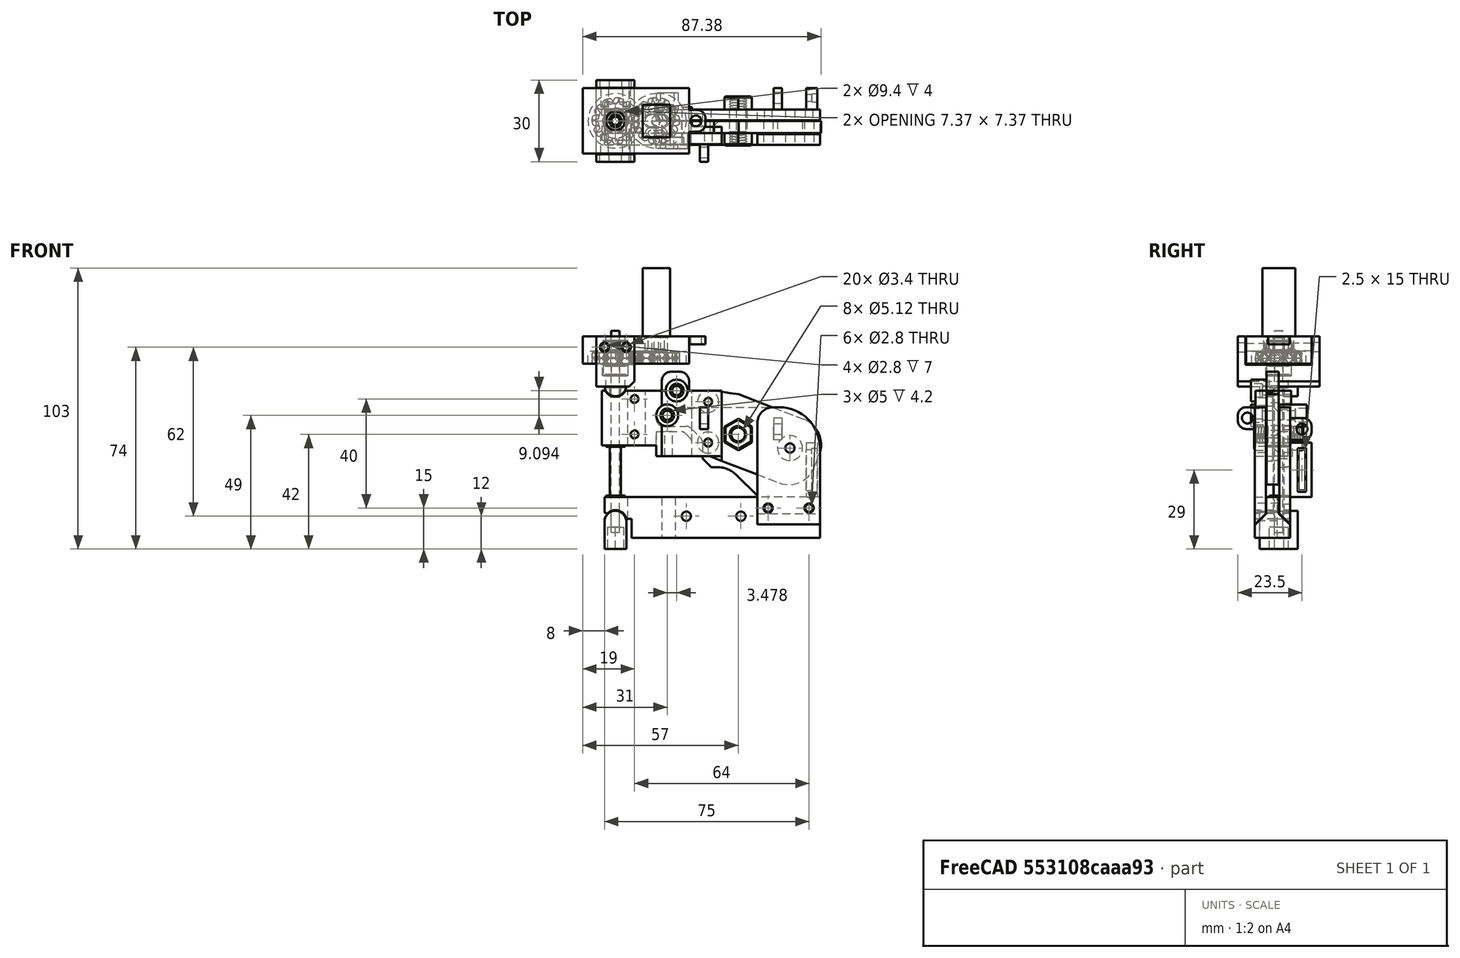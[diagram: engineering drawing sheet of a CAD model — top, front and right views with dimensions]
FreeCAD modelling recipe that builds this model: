
FCSTD DOCUMENT  (FreeCAD 0.17R13528 (Git))
Label: guillotine
License: All rights reserved
LicenseURL: http://en.wikipedia.org/wiki/All_rights_reserved
objects: Part::Cylinder×82, Part::MultiFuse×54, Part::Cut×51, Part::Box×48, Part::Feature×20, Part::Chamfer×14, Part::Fillet×10, Part::Mirroring×9, Part::MultiCommon×3, App::DocumentObjectGroup×3, Part::Fuse×2
note: 293 computed .brp shape members not serialized (recipe doc carries the construction recipe); baked Part::Feature solids carry a one-line shape summary decoded from their .brp

FEATURE [Part::Box] Box001027033  label="Cube053"
  AttacherType = Attacher::AttachEngine3D
  Height = 25
  Length = 40
  Placement = pos=(32,-4.5,-33) rot=(0,1,0;0.366519rad)
  Width = 4.5
FEATURE [Part::Box] Box001027045154  label="Cube202"
  AttacherType = Attacher::AttachEngine3D
  Height = 24
  Length = 47
  Placement = pos=(-5,-4.5,-34) rot=(0,1,0;0rad)
  Width = 4.5
FEATURE [Part::Box] Box001027045159  label="Cube207"
  AttacherType = Attacher::AttachEngine3D
  Height = 10
  Length = 20
  Placement = pos=(29,-6,-9) rot=(0,1,0;0.139626rad)
  Width = 10
FEATURE [Part::Cylinder] Cylinder210  label="cutter-fit-cylinder001"
  Angle = 360
  AttacherType = Attacher::AttachEngine3D
  Height = 21
  Placement = pos=(45,5,-26) rot=(1,0,0;1.5708rad)
  Radius = 3.2
FEATURE [Part::Box] Box001027045161  label="Cube209"
  AttacherType = Attacher::AttachEngine3D
  Height = 15
  Length = 30
  Placement = pos=(-10,-7,-57) rot=(0,0,1;0rad)
  Width = 15
FEATURE [Part::Feature] Part__Feature069020  label="M6 thread016"
  Placement = pos=(45,-4,-26) rot=(0.935113,0.250563,-0.250563;1.63783rad)
  shape: bbox 10 x 5.798 x 11.55 mm, 23 faces (baked)
FEATURE [Part::MultiFuse] Fusion112112  label="move-arm-1"
  Shapes = -> [Box001027033,Box001027045154]
FEATURE [Part::Cut] Cut190  label="move-arm-2"
  Base = -> Fusion112112
  Tool = -> Box001027045159
FEATURE [Part::Cut] Cut191  label="move-arm-3"
  Base = -> Cut190
  Tool = -> Cylinder210
FEATURE [Part::MultiFuse] Fusion112113  label="move-arm-4"
  Shapes = -> [Cut191,Part__Feature069020]
FEATURE [Part::Cylinder] Cylinder214  label="bearing-fit-cylinder001"
  Angle = 360
  AttacherType = Attacher::AttachEngine3D
  Height = 21
  Placement = pos=(64,5,-31) rot=(1,0,0;1.5708rad)
  Radius = 4.6
FEATURE [Part::Cut] Cut192  label="move-arm-5"
  Base = -> Fusion112113
  Placement = pos=(-6.44714,0,-21.2943) rot=(0,-1,0;0.314159rad)
  Tool = -> Cylinder214
FEATURE [Part::Cut] Cut193  label="move-arm-6"
  Base = -> Cut192
  Placement = pos=(12.7119,0,18.2598) rot=(0,1,0;0.314159rad)
  Tool = -> Box001027045161
FEATURE [Part::Box] Box001027045166  label="Cube214"
  AttacherType = Attacher::AttachEngine3D
  Height = 35
  Length = 46
  Placement = pos=(-7,-7,-36) rot=(0,0,1;0rad)
  Width = 32
FEATURE [Part::Box] Box001027045167  label="Cube215"
  AttacherType = Attacher::AttachEngine3D
  Height = 44
  Length = 12
  Placement = pos=(28,-2.25,-41) rot=(0,0,1;0rad)
  Width = 31
FEATURE [Part::Cut] Cut202
  Base = -> Box001027045166
  Tool = -> Box001027045167
FEATURE [Part::Cut] Cut208
  Base = -> Cut193
  Tool = -> Cut202
FEATURE [Part::Box] Box001027045174  label="Cube222"
  AttacherType = Attacher::AttachEngine3D
  Height = 24
  Length = 22
  Placement = pos=(17,-8.5,-34) rot=(0,0,1;0rad)
  Width = 4
FEATURE [Part::Cylinder] Cylinder226  label="M3-clearance001"
  Angle = 360
  AttacherType = Attacher::AttachEngine3D
  Height = 20
  Placement = pos=(34,5,-14) rot=(1,0,0;1.5708rad)
  Radius = 1.7
FEATURE [Part::Cylinder] Cylinder227  label="M3-clearance002"
  Angle = 360
  AttacherType = Attacher::AttachEngine3D
  Height = 20
  Placement = pos=(34,5,-29) rot=(1,0,0;1.5708rad)
  Radius = 1.7
FEATURE [Part::Cylinder] Cylinder230  label="M3-tap005"
  Angle = 360
  AttacherType = Attacher::AttachEngine3D
  Height = 20
  Placement = pos=(34,5,-14) rot=(1,0,0;1.5708rad)
  Radius = 1.4
FEATURE [Part::Cylinder] Cylinder231  label="M3-tap006"
  Angle = 360
  AttacherType = Attacher::AttachEngine3D
  Height = 20
  Placement = pos=(34,5,-29) rot=(1,0,0;1.5708rad)
  Radius = 1.4
FEATURE [Part::MultiFuse] Fusion112121
  Shapes = -> [Cylinder226,Cylinder227]
FEATURE [Part::MultiFuse] Fusion112123
  Shapes = -> [Cylinder230,Cylinder231]
FEATURE [Part::Cut] Cut210  label="cutter-arm-1"
  Base = -> Cut208
  Tool = -> Fusion112121
FEATURE [Part::Chamfer] Chamfer021
  Base = -> Cut210
  Edges = 1 edges r=2.2: [Edge107]
FEATURE [Part::Chamfer] Chamfer022
  Base = -> Chamfer021
  Edges = 3 edges r=2.2: [Edge5,Edge20,Edge21]
FEATURE [Part::Fillet] Fillet041  label="cutting-arm"
  Base = -> Chamfer022
  Edges = 2 edges r=10: [Edge49,Edge58]
FEATURE [Part::Box] Box001027011  label="Cube031"
  AttacherType = Attacher::AttachEngine3D
  Height = 43
  Length = 40
  Placement = pos=(35,0.2,-59) rot=(0,0,1;0rad)
  Width = 4
FEATURE [Part::Cylinder] Cylinder074  label="cutter-fit-cylinder"
  Angle = 360
  AttacherType = Attacher::AttachEngine3D
  Height = 21
  Placement = pos=(45,5,-26) rot=(1,0,0;1.5708rad)
  Radius = 3.2
FEATURE [Part::Box] Box001027030  label="Cube050"
  AttacherType = Attacher::AttachEngine3D
  Height = 12
  Length = 25
  Placement = pos=(18,-5,-42) rot=(0,0,1;0rad)
  Width = 9.5
FEATURE [Part::Chamfer] Chamfer010
  Base = -> Box001027030
  Edges = 2 edges r=5: [Edge2,Edge6]
FEATURE [Part::Fillet] Fillet025  label="Adjuster-hole"
  Base = -> Chamfer010
  Edges = 4 edges r=3: [Edge2,Edge10,Edge17,Edge18]
  Placement = pos=(-11,0,7) rot=(0,0,1;0rad)
FEATURE [Part::Box] Box001027045147  label="Cube195"
  AttacherType = Attacher::AttachEngine3D
  Height = 43
  Length = 23
  Placement = pos=(52,-8.8,-59) rot=(0,0,1;0rad)
  Width = 4
FEATURE [Part::Box] Box001027045148  label="Cube196"
  AttacherType = Attacher::AttachEngine3D
  Height = 26
  Length = 29
  Placement = pos=(23,-2,-64) rot=(0,0,1;0rad)
  Width = 10
FEATURE [Part::Box] Box001027045149  label="Cube197"
  AttacherType = Attacher::AttachEngine3D
  Height = 15
  Length = 79
  Placement = pos=(-4,-8.8,-64) rot=(0,0,1;0rad)
  Width = 13
FEATURE [Part::Cut] Cut172
  Base = -> Box001027011
  Tool = -> Box001027045148
FEATURE [Part::Cylinder] Cylinder197  label="rocker-cut001"
  Angle = 360
  AttacherType = Attacher::AttachEngine3D
  Height = 18
  Placement = pos=(0,7,-58) rot=(1,0,0;1.5708rad)
  Radius = 4.2
FEATURE [Part::Box] Box001027045150  label="Cube198"
  AttacherType = Attacher::AttachEngine3D
  Height = 15
  Length = 20
  Placement = pos=(-14,-11.8,-72) rot=(0,0,1;0rad)
  Width = 18
FEATURE [Part::MultiFuse] Fusion112098
  Shapes = -> [Box001027045150,Cylinder197]
FEATURE [Part::Cut] Cut173
  Base = -> Box001027045149
  Tool = -> Fusion112098
FEATURE [Part::Chamfer] Chamfer017
  Base = -> Cut173
  Edges = 1 edges r=2: [Edge4]
FEATURE [Part::Box] Box001027045151  label="Cube199"
  AttacherType = Attacher::AttachEngine3D
  Height = 43
  Length = 41
  Placement = pos=(35,0,-59) rot=(0,0,1;0rad)
  Width = 7
FEATURE [Part::Box] Box001027045152  label="Cube200"
  AttacherType = Attacher::AttachEngine3D
  Height = 43
  Length = 25
  Placement = pos=(52,-10.6,-59) rot=(0,0,1;0rad)
  Width = 6
FEATURE [Part::Box] Box001027045153  label="Cube201"
  AttacherType = Attacher::AttachEngine3D
  Height = 26
  Length = 29
  Placement = pos=(23,-2,-64) rot=(0,0,1;0rad)
  Width = 10
FEATURE [Part::Cut] Cut174
  Base = -> Box001027045151
  Tool = -> Box001027045153
FEATURE [Part::MultiFuse] Fusion112099
  Shapes = -> [Box001027045152,Cut174]
FEATURE [Part::Cut] Cut175
  Base = -> Chamfer017
  Tool = -> Fusion112099
FEATURE [Part::Cylinder] Cylinder198  label="Cylinder242"
  Angle = 360
  AttacherType = Attacher::AttachEngine3D
  Height = 20
  Placement = pos=(56,8,-54) rot=(1,0,0;1.5708rad)
  Radius = 1.7
FEATURE [Part::Cylinder] Cylinder199  label="Cylinder243"
  Angle = 360
  AttacherType = Attacher::AttachEngine3D
  Height = 20
  Placement = pos=(71,8,-54) rot=(1,0,0;1.5708rad)
  Radius = 1.7
FEATURE [Part::Cylinder] Cylinder200  label="Cylinder244"
  Angle = 360
  AttacherType = Attacher::AttachEngine3D
  Height = 20
  Placement = pos=(56,8,-54) rot=(1,0,0;1.5708rad)
  Radius = 1.7
FEATURE [Part::Cylinder] Cylinder201  label="Cylinder245"
  Angle = 360
  AttacherType = Attacher::AttachEngine3D
  Height = 20
  Placement = pos=(71,8,-54) rot=(1,0,0;1.5708rad)
  Radius = 1.7
FEATURE [Part::Cylinder] Cylinder202  label="Cylinder246"
  Angle = 360
  AttacherType = Attacher::AttachEngine3D
  Height = 20
  Placement = pos=(56,8,-54) rot=(1,0,0;1.5708rad)
  Radius = 1.4
FEATURE [Part::Cylinder] Cylinder203  label="Cylinder247"
  Angle = 360
  AttacherType = Attacher::AttachEngine3D
  Height = 20
  Placement = pos=(71,8,-54) rot=(1,0,0;1.5708rad)
  Radius = 1.4
FEATURE [Part::MultiFuse] Fusion112100
  Placement = pos=(0,0,1) rot=(0,0,1;0rad)
  Shapes = -> [Cylinder198,Cylinder199]
FEATURE [Part::MultiFuse] Fusion112101
  Placement = pos=(0,0,1) rot=(0,0,1;0rad)
  Shapes = -> [Cylinder200,Cylinder201]
FEATURE [Part::MultiFuse] Fusion112102
  Placement = pos=(0,0,1) rot=(0,0,1;0rad)
  Shapes = -> [Cylinder202,Cylinder203]
FEATURE [Part::Cut] Cut176
  Base = -> Cut175
  Tool = -> Fusion112100
FEATURE [Part::Cut] Cut177
  Base = -> Box001027045147
  Tool = -> Fusion112101
FEATURE [Part::Cut] Cut178
  Base = -> Cut172
  Tool = -> Fusion112102
FEATURE [Part::Cylinder] Cylinder204  label="Cylinder248"
  Angle = 360
  AttacherType = Attacher::AttachEngine3D
  Height = 20
  Placement = pos=(26,8,-54) rot=(1,0,0;1.5708rad)
  Radius = 1.7
FEATURE [Part::Cylinder] Cylinder205  label="Cylinder249"
  Angle = 360
  AttacherType = Attacher::AttachEngine3D
  Height = 20
  Placement = pos=(46,8,-54) rot=(1,0,0;1.5708rad)
  Radius = 1.7
FEATURE [Part::MultiFuse] Fusion112103
  Placement = pos=(0,0,-2) rot=(0,0,1;0rad)
  Shapes = -> [Cylinder204,Cylinder205]
FEATURE [Part::Cut] Cut179
  Base = -> Cut176
  Tool = -> Fusion112103
FEATURE [Part::Box] Box001027045157  label="Cube205"
  AttacherType = Attacher::AttachEngine3D
  Height = 18
  Length = 40
  Placement = pos=(15,0.2,-34) rot=(0,0,1;0rad)
  Width = 4
FEATURE [Part::MultiFuse] Fusion112104
  Shapes = -> [Cut178,Box001027045157]
FEATURE [Part::Chamfer] Chamfer019
  Base = -> Fusion112104
  Edges = 1 edges r=3.9: [Edge12]
FEATURE [Part::Chamfer] Chamfer020
  Base = -> Chamfer019
  Edges = 1 edges r=10.5: [Edge31]
FEATURE [Part::Cut] Cut180
  Base = -> Chamfer020
  Tool = -> Fillet025
FEATURE [Part::Cylinder] Cylinder209  label="Cylinder253"
  Angle = 360
  AttacherType = Attacher::AttachEngine3D
  Height = 30
  Placement = pos=(19.5,2,-70) rot=(0,0,1;0rad)
  Radius = 2.5
FEATURE [Part::Box] Box001027045160  label="Cube208"
  AttacherType = Attacher::AttachEngine3D
  Height = 21
  Length = 5
  Placement = pos=(17,2,-68) rot=(0,0,1;0rad)
  Width = 10
FEATURE [Part::MultiFuse] Fusion112106
  Shapes = -> [Cylinder209,Box001027045160]
FEATURE [Part::Cut] Cut184
  Base = -> Cut179
  Tool = -> Fusion112106
FEATURE [Part::Cut] Cut186
  Base = -> Cut180
  Tool = -> Cylinder074
FEATURE [Part::Feature] Part__Feature069021  label="M6 thread017"
  Placement = pos=(45,-4,-26) rot=(0.935113,0.250563,-0.250563;1.63783rad)
  shape: bbox 10 x 5.798 x 11.55 mm, 23 faces (baked)
FEATURE [Part::Mirroring] Part__Mirroring014  label="M6 thread017 (Mirror #14)"
  Base = (0,0,0)
  Normal = (0,1,0)
  Source = -> Part__Feature069021
FEATURE [Part::MultiFuse] Fusion112109
  Shapes = -> [Cut186,Part__Mirroring014]
FEATURE [Part::Cylinder] Cylinder211  label="Cylinder254"
  Angle = 360
  AttacherType = Attacher::AttachEngine3D
  Height = 74
  Placement = pos=(0,0,-62) rot=(0,0,1;0rad)
  Radius = 2
FEATURE [Part::Box] Box001027045163  label="Cube211"
  AttacherType = Attacher::AttachEngine3D
  Height = 60
  Length = 10
  Placement = pos=(-10,-2,-57) rot=(0,0,1;0rad)
  Width = 4
FEATURE [Part::MultiFuse] Fusion112110
  Placement = pos=(2.5,0,0) rot=(0,0,1;0rad)
  Shapes = -> [Cylinder211,Box001027045163]
FEATURE [Part::Cut] Cut189  label="base-and-mount-b"
  Base = -> Cut184
  Tool = -> Fusion112110
FEATURE [Part::Cylinder] Cylinder222  label="bearing-fit-cylinder002"
  Angle = 360
  AttacherType = Attacher::AttachEngine3D
  Height = 21
  Placement = pos=(64,5,-31) rot=(1,0,0;1.5708rad)
  Radius = 1.7
FEATURE [Part::Cylinder] Cylinder223  label="bearing-fit-cylinder003"
  Angle = 360
  AttacherType = Attacher::AttachEngine3D
  Height = 21
  Placement = pos=(64,5,-31) rot=(1,0,0;1.5708rad)
  Radius = 1.7
FEATURE [Part::Cut] Cut200
  Base = -> Fusion112109
  Tool = -> Cylinder222
FEATURE [Part::Cut] Cut201
  Base = -> Cut177
  Tool = -> Cylinder223
FEATURE [Part::Fillet] Fillet033
  Base = -> Cut200
  Edges = 1 edges r=15: [Edge111]
FEATURE [Part::Fillet] Fillet034
  Base = -> Cut201
  Edges = 1 edges r=15: [Edge12]
FEATURE [Part::Fillet] Fillet035
  Base = -> Fillet033
  Edges = 2 edges r=2.5: [Edge63,Edge65]
FEATURE [Part::Fillet] Fillet038  label="bearing-support-1a"
  Base = -> Fillet034
  Edges = 1 edges r=6: [Edge17]
FEATURE [Part::Fillet] Fillet039  label="bearing-support-2a"
  Base = -> Fillet035
  Edges = 1 edges r=10: [Edge65]
FEATURE [Part::Chamfer] Chamfer026
  Base = -> Cut189
  Edges = 1 edges r=4: [Edge73]
FEATURE [Part::Chamfer] Chamfer027  label="base-and-mount"
  Base = -> Chamfer026
  Edges = 1 edges r=4: [Edge34]
FEATURE [Part::Chamfer] Chamfer028  label="bearing-support-1"
  Base = -> Fillet038
  Edges = 1 edges r=3.9: [Edge21]
FEATURE [Part::Chamfer] Chamfer029  label="bearing-support-2a001"
  Base = -> Fillet039
  Edges = 1 edges r=3.9: [Edge5]
FEATURE [Part::Box] Box  label="Cube"
  AttacherType = Attacher::AttachEngine3D
  Height = 20
  Length = 4
  Placement = pos=(0,-10,-10) rot=(0,0,1;0rad)
  Width = 20
FEATURE [Part::Feature] Part__Feature027  label="1310"
  Placement = pos=(2,0,0) rot=(0,0,1;0rad)
  shape: bbox 13.32 x 18 x 18 mm, 178 faces (baked)
FEATURE [Part::Cylinder] Cylinder
  Angle = 360
  AttacherType = Attacher::AttachEngine3D
  Height = 25
  Placement = pos=(-4,0,0) rot=(0,1,0;1.5708rad)
  Radius = 5
FEATURE [Part::Cylinder] Cylinder001
  Angle = 360
  AttacherType = Attacher::AttachEngine3D
  Height = 10
  Placement = pos=(-2,0,0) rot=(0,1,0;1.5708rad)
  Radius = 1.7
FEATURE [Part::MultiFuse] Fusion
  Shapes = -> [Part__Feature027,Cylinder]
FEATURE [Part::MultiCommon] Common  label="gear-blank"
  Shapes = -> [Fusion,Box]
FEATURE [Part::Feature] Part__Feature028  label="1310001"
  Placement = pos=(2,0,0) rot=(0,0,1;0rad)
  shape: bbox 13.32 x 18 x 18 mm, 178 faces (baked)
FEATURE [Part::Cut] Cut  label="shaft-gear-a"
  Base = -> Common
  Placement = pos=(0,0,0) rot=(0,-1,0;1.5708rad)
  Tool = -> Cylinder001
FEATURE [Part::Box] Box002  label="Cube002"
  AttacherType = Attacher::AttachEngine3D
  Height = 10
  Length = 15
  Placement = pos=(-4,-6,1) rot=(0,0,1;0rad)
  Width = 10
FEATURE [Part::Cylinder] Cylinder002
  Angle = 360
  AttacherType = Attacher::AttachEngine3D
  Height = 25
  Placement = pos=(-4,0,0) rot=(0,1,0;1.5708rad)
  Radius = 5
FEATURE [Part::MultiFuse] Fusion001
  Shapes = -> [Part__Feature028,Cylinder002]
FEATURE [Part::Cylinder] Cylinder003
  Angle = 360
  AttacherType = Attacher::AttachEngine3D
  Height = 10
  Placement = pos=(-2,0,0) rot=(0,1,0;1.5708rad)
  Radius = 1.8
FEATURE [Part::Cut] Cut001
  Base = -> Cylinder003
  Tool = -> Box002
FEATURE [Part::Fuse] Fusion003
FEATURE [Part::Cylinder] Cylinder012
  Angle = 360
  AttacherType = Attacher::AttachEngine3D
  Height = 10
  Placement = pos=(5,-4.5,0) rot=(0,1,0;1.5708rad)
  Radius = 0.8
FEATURE [Part::Fuse] Fusion048  label="motor"
  Base = -> Cylinder012
  Placement = pos=(15,0,0) rot=(0,-1,0;1.5708rad)
  Tool = -> Fusion003
FEATURE [Part::Box] Box001  label="Cube001"
  AttacherType = Attacher::AttachEngine3D
  Height = 20
  Length = 4
  Placement = pos=(0,-10,-10) rot=(0,0,1;0rad)
  Width = 20
FEATURE [Part::MultiCommon] Common001  label="gear-blank001"
  Shapes = -> [Fusion001,Box001]
FEATURE [Part::Cut] Cut002  label="motor-gear"
  Base = -> Common001
  Placement = pos=(15,0,4) rot=(0,1,0;1.5708rad)
  Tool = -> Cut001
FEATURE [Part::Feature] Part__Feature035  label="423001001"
  Placement = pos=(0,0,-2) rot=(0,0,1;3.74342rad)
  shape: bbox 9 x 9 x 4 mm, 22 faces (baked)
FEATURE [Part::Feature] Part__Feature066  label="212001001001"
  Placement = pos=(0,0,0) rot=(0.905883,0.423527,0;3.14159rad)
  shape: bbox 7 x 7 x 0.5 mm, 6 faces (baked)
FEATURE [Part::Cylinder] Cylinder013
  Angle = 360
  AttacherType = Attacher::AttachEngine3D
  Height = 74
  Placement = pos=(0,0,-62) rot=(0,0,1;0rad)
  Radius = 1.5
FEATURE [Part::Cylinder] Cylinder014
  Angle = 360
  AttacherType = Attacher::AttachEngine3D
  Height = 8
  Placement = pos=(0,0,1) rot=(0,0,1;0rad)
  Radius = 4
FEATURE [Part::Box] Box003  label="Cube003"
  AttacherType = Attacher::AttachEngine3D
  Height = 10
  Length = 10
  Placement = pos=(-12.85,-5,0) rot=(0,0,1;0rad)
  Width = 10
FEATURE [Part::Feature] Box001001
  Placement = pos=(-2.09487,-13.6284,0) rot=(0,0,1;1.0472rad)
  shape: bbox 13.66 x 13.66 x 10 mm, 6 faces (baked)
FEATURE [Part::Feature] Box001002
  Placement = pos=(10.7551,-8.62843,0) rot=(0,0,1;2.0944rad)
  shape: bbox 13.66 x 13.66 x 10 mm, 6 faces (baked)
FEATURE [Part::Feature] Box001003
  Placement = pos=(12.85,5,0) rot=(0,0,1;3.14159rad)
  shape: bbox 10 x 10 x 10 mm, 6 faces (baked)
FEATURE [Part::Feature] Box001004
  Placement = pos=(2.09487,13.6284,0) rot=(0,0,1;4.18879rad)
  shape: bbox 13.66 x 13.66 x 10 mm, 6 faces (baked)
FEATURE [Part::Feature] Box001005
  Placement = pos=(-10.7551,8.62843,0) rot=(0,0,-1;1.0472rad)
  shape: bbox 13.66 x 13.66 x 10 mm, 6 faces (baked)
FEATURE [Part::MultiFuse] Fusion049
  Shapes = -> [Box003,Box001005,Box001001,Box001002,Box001003,Box001004]
FEATURE [Part::Cut] Cut003  label="m3-nut"
  Base = -> Cylinder014
  Placement = pos=(0,0,1) rot=(0,0,1;0rad)
  Tool = -> Fusion049
FEATURE [Part::Feature] Part__Feature067  label="423001001001"
  Placement = pos=(0,0,7) rot=(0,0,1;3.74342rad)
  shape: bbox 9 x 9 x 4 mm, 22 faces (baked)
FEATURE [Part::Cylinder] Cylinder015
  Angle = 360
  AttacherType = Attacher::AttachEngine3D
  Height = 100
  Placement = pos=(0,0,-12) rot=(0,0,1;0rad)
  Radius = 1.7
FEATURE [Part::MultiFuse] Fusion050
  Shapes = -> [Cylinder015,Cut003]
FEATURE [Part::Cut] Cut004  label="shaft-gear"
  Base = -> Cut
  Tool = -> Fusion050
FEATURE [Part::Box] Box001006  label="Cube004"
  AttacherType = Attacher::AttachEngine3D
  Height = 10
  Length = 39
  Placement = pos=(-12,-12,0) rot=(0,0,1;0rad)
  Width = 24
FEATURE [Part::Cylinder] Cylinder016
  Angle = 360
  AttacherType = Attacher::AttachEngine3D
  Height = 30
  Placement = pos=(0,0,-12) rot=(0,0,1;0rad)
  Radius = 3.5
FEATURE [Part::Cylinder] Cylinder017
  Angle = 360
  AttacherType = Attacher::AttachEngine3D
  Height = 30
  Placement = pos=(0,0,-21.5) rot=(0,0,1;0rad)
  Radius = 4.7
FEATURE [Part::Cylinder] Cylinder018
  Angle = 360
  AttacherType = Attacher::AttachEngine3D
  Height = 30
  Placement = pos=(0,0,-25.5) rot=(0,0,1;0rad)
  Radius = 10
FEATURE [Part::Cylinder] Cylinder019
  Angle = 360
  AttacherType = Attacher::AttachEngine3D
  Height = 30
  Placement = pos=(16,0,-25.5) rot=(0,0,1;0rad)
  Radius = 10
FEATURE [Part::Cylinder] Cylinder020
  Angle = 360
  AttacherType = Attacher::AttachEngine3D
  Height = 30
  Placement = pos=(17,0,-12.5) rot=(0,0,1;0rad)
  Radius = 2.1
FEATURE [Part::Cylinder] Cylinder021
  Angle = 360
  AttacherType = Attacher::AttachEngine3D
  Height = 30
  Placement = pos=(17,-4.5,-12.5) rot=(0,0,1;0rad)
  Radius = 1
FEATURE [Part::Cylinder] Cylinder022
  Angle = 360
  AttacherType = Attacher::AttachEngine3D
  Height = 30
  Placement = pos=(17,4.5,-12.5) rot=(0,0,1;0rad)
  Radius = 1
FEATURE [Part::Cylinder] Cylinder023
  Angle = 360
  AttacherType = Attacher::AttachEngine3D
  Height = 30
  Placement = pos=(13,0,-12.5) rot=(0,0,1;0rad)
  Radius = 2.1
FEATURE [Part::Cylinder] Cylinder024
  Angle = 360
  AttacherType = Attacher::AttachEngine3D
  Height = 30
  Placement = pos=(13,-4.5,-12.5) rot=(0,0,1;0rad)
  Radius = 1
FEATURE [Part::Cylinder] Cylinder025
  Angle = 360
  AttacherType = Attacher::AttachEngine3D
  Height = 30
  Placement = pos=(13,4.5,-12.5) rot=(0,0,1;0rad)
  Radius = 1
FEATURE [Part::Box] Box001007  label="Cube005"
  AttacherType = Attacher::AttachEngine3D
  Height = 27
  Length = 4
  Placement = pos=(13,-2.1,-11) rot=(0,0,1;0rad)
  Width = 4.2
FEATURE [Part::Box] Box001008  label="Cube006"
  AttacherType = Attacher::AttachEngine3D
  Height = 27
  Length = 4
  Placement = pos=(13,-5.5,-11) rot=(0,0,1;0rad)
  Width = 2
FEATURE [Part::Box] Box001009  label="Cube007"
  AttacherType = Attacher::AttachEngine3D
  Height = 27
  Length = 4
  Placement = pos=(13,3.5,-11) rot=(0,0,1;0rad)
  Width = 2
FEATURE [Part::MultiFuse] Fusion052  label="motor-slots"
  Shapes = -> [Box001009,Cylinder021,Cylinder022,Box001007,Cylinder020,Cylinder023,Cylinder024,Box001008,Cylinder025]
FEATURE [Part::Cylinder] Cylinder026
  Angle = 360
  AttacherType = Attacher::AttachEngine3D
  Height = 30
  Placement = pos=(15,0,-25.5) rot=(0,0,1;0rad)
  Radius = 10
FEATURE [Part::MultiFuse] Fusion053  label="gearbox-cavity-1"
  Shapes = -> [Cylinder019,Cylinder016,Cylinder017,Cylinder018,Cylinder026]
FEATURE [Part::MultiFuse] Fusion054  label="gearbox-cavity-2"
  Shapes = -> [Fusion053,Fusion052]
FEATURE [Part::Cut] Cut005  label="gearbox-1"
  Base = -> Box001006
  Tool = -> Fusion054
FEATURE [Part::Chamfer] Chamfer  label="gearbox-2"
  Base = -> Cut005
  Edges = 10 edges r=1: [Edge47,Edge50,Edge52,Edge54,Edge55,Edge58,Edge60,Edge62,Edge64,Edge65]
FEATURE [Part::Box] Box001010  label="Cube008"
  AttacherType = Attacher::AttachEngine3D
  Height = 8
  Length = 14
  Placement = pos=(-7,-15,-8.5) rot=(0,0,1;0rad)
  Width = 30
FEATURE [Part::Box] Box001011  label="Cube009"
  AttacherType = Attacher::AttachEngine3D
  Height = 11
  Length = 14
  Placement = pos=(-7,-15,-1) rot=(0,0,1;0rad)
  Width = 2.8
FEATURE [Part::Box] Box001012  label="Cube010"
  AttacherType = Attacher::AttachEngine3D
  Height = 11
  Length = 14
  Placement = pos=(-7,12.2,-1) rot=(0,0,1;0rad)
  Width = 2.8
FEATURE [Part::MultiFuse] Fusion055  label="bearing-clamp-1"
  Shapes = -> [Box001010,Box001012,Box001011]
FEATURE [Part::Cylinder] Cylinder027  label="M3-tap-1"
  Angle = 360
  AttacherType = Attacher::AttachEngine3D
  Height = 19
  Placement = pos=(-4,24,6) rot=(1,0,0;1.5708rad)
  Radius = 1.4
FEATURE [Part::Cylinder] Cylinder028  label="M3-tap-2"
  Angle = 360
  AttacherType = Attacher::AttachEngine3D
  Height = 19
  Placement = pos=(4,24,6) rot=(1,0,0;1.5708rad)
  Radius = 1.4
FEATURE [Part::Cylinder] Cylinder029  label="M3-clear-1"
  Angle = 360
  AttacherType = Attacher::AttachEngine3D
  Height = 19
  Placement = pos=(-4,24,6) rot=(1,0,0;1.5708rad)
  Radius = 1.7
FEATURE [Part::Cylinder] Cylinder030  label="M3-clear-2"
  Angle = 360
  AttacherType = Attacher::AttachEngine3D
  Height = 19
  Placement = pos=(4,24,6) rot=(1,0,0;1.5708rad)
  Radius = 1.7
FEATURE [Part::Cylinder] Cylinder031  label="M3-tap-003"
  Angle = 360
  AttacherType = Attacher::AttachEngine3D
  Height = 19
  Placement = pos=(-4,24,6) rot=(1,0,0;1.5708rad)
  Radius = 1.4
FEATURE [Part::Cylinder] Cylinder032  label="M3-tap-004"
  Angle = 360
  AttacherType = Attacher::AttachEngine3D
  Height = 19
  Placement = pos=(4,24,6) rot=(1,0,0;1.5708rad)
  Radius = 1.4
FEATURE [Part::Cylinder] Cylinder033  label="M3-clear-003"
  Angle = 360
  AttacherType = Attacher::AttachEngine3D
  Height = 19
  Placement = pos=(4,24,6) rot=(1,0,0;1.5708rad)
  Radius = 1.7
FEATURE [Part::Cylinder] Cylinder034  label="M3-clear-004"
  Angle = 360
  AttacherType = Attacher::AttachEngine3D
  Height = 19
  Placement = pos=(-4,24,6) rot=(1,0,0;1.5708rad)
  Radius = 1.7
FEATURE [Part::Mirroring] Part__Mirroring  label="M3-tap-003 (Mirror #1)"
  Base = (0,0,0)
  Normal = (0,1,0)
  Source = -> Cylinder031
FEATURE [Part::Mirroring] Part__Mirroring001  label="M3-tap-004 (Mirror #2)"
  Base = (0,0,0)
  Normal = (0,1,0)
  Source = -> Cylinder032
FEATURE [Part::Mirroring] Part__Mirroring002  label="M3-clear-003 (Mirror #3)"
  Base = (0,0,0)
  Normal = (0,1,0)
  Source = -> Cylinder033
FEATURE [Part::Mirroring] Part__Mirroring003  label="M3-clear-004 (Mirror #4)"
  Base = (0,0,0)
  Normal = (0,1,0)
  Source = -> Cylinder034
FEATURE [Part::MultiFuse] Fusion056  label="M3-tap-a"
  Shapes = -> [Cylinder027,Cylinder028,Part__Mirroring,Part__Mirroring001]
FEATURE [Part::MultiFuse] Fusion057  label="M3-clear-a"
  Shapes = -> [Cylinder029,Cylinder030,Part__Mirroring002,Part__Mirroring003]
FEATURE [Part::Cut] Cut006  label="bearing-clamp-2"
  Base = -> Fusion055
  Tool = -> Fusion057
FEATURE [Part::Cut] Cut007  label="gearbox-3"
  Base = -> Chamfer
  Tool = -> Fusion056
FEATURE [Part::Cylinder] Cylinder035
  Angle = 360
  AttacherType = Attacher::AttachEngine3D
  Height = 30
  Placement = pos=(0,0,-4.5) rot=(0,0,1;0rad)
  Radius = 4.7
FEATURE [Part::Cylinder] Cylinder036
  Angle = 360
  AttacherType = Attacher::AttachEngine3D
  Height = 30
  Placement = pos=(0,0,-9) rot=(0,0,1;0rad)
  Radius = 3.5
FEATURE [Part::Cylinder] Cylinder061  label="rocker-1"
  Angle = 360
  AttacherType = Attacher::AttachEngine3D
  Height = 14
  Placement = pos=(0,7,-52) rot=(1,0,0;1.5708rad)
  Radius = 4
FEATURE [Part::Box] Box001026  label="Cube024"
  AttacherType = Attacher::AttachEngine3D
  Height = 10
  Length = 8
  Placement = pos=(-4,-7,-62) rot=(0,0,1;0rad)
  Width = 14
FEATURE [Part::MultiFuse] Fusion077  label="rocker-2"
  Shapes = -> [Cylinder061,Box001026]
FEATURE [Part::Cylinder] Cylinder063
  Angle = 360
  AttacherType = Attacher::AttachEngine3D
  Height = 62
  Placement = pos=(0,0,-75) rot=(0,0,1;0rad)
  Radius = 1.5
FEATURE [Part::Cut] Cut032  label="rocker-3"
  Base = -> Fusion077
  Tool = -> Cylinder063
FEATURE [Part::Cylinder] Cylinder064
  Angle = 360
  AttacherType = Attacher::AttachEngine3D
  Height = 20
  Placement = pos=(0,0,-74) rot=(0,0,1;0rad)
  Radius = 4
FEATURE [Part::Box] Box001027  label="Cube025"
  AttacherType = Attacher::AttachEngine3D
  Height = 25
  Length = 10
  Placement = pos=(3,-5,-77) rot=(0,0,1;0rad)
  Width = 10
FEATURE [Part::Cylinder] Cylinder065
  Angle = 360
  AttacherType = Attacher::AttachEngine3D
  Height = 62
  Placement = pos=(0,0,-59) rot=(0,0,1;0rad)
  Radius = 2
FEATURE [Part::Cylinder] Cylinder066  label="rocker-005"
  Angle = 360
  AttacherType = Attacher::AttachEngine3D
  Height = 14
  Placement = pos=(0,7,-8) rot=(1,0,0;1.5708rad)
  Radius = 4
FEATURE [Part::MultiFuse] Fusion080  label="bearing-nut"
  Shapes = -> [Cylinder035,Cylinder036]
FEATURE [Part::Cut] Cut035
  Base = -> Cylinder066
  Tool = -> Cylinder065
FEATURE [Part::MultiFuse] Fusion081
  Shapes = -> [Cut006,Cut035]
FEATURE [Part::Cut] Cut036  label="bearing-clamp-003"
  Base = -> Fusion081
  Tool = -> Fusion080
FEATURE [Part::Cylinder] Cylinder069  label="1251-spring"
  Angle = 360
  AttacherType = Attacher::AttachEngine3D
  Height = 18.5
  Placement = pos=(0,0,-49) rot=(0,0,1;0rad)
  Radius = 2
FEATURE [Part::Chamfer] Chamfer011  label="bearing-clamp"
  Base = -> Cut036
  Edges = 1 edges r=2: [Edge43]
FEATURE [Part::Chamfer] Chamfer014  label="gearbox-004"
  Base = -> Cut007
  Edges = 5 edges r=0.5: [Edge16,Edge17,Edge18,Edge19,Edge20]
FEATURE [Part::Feature] Box001027038
  Placement = pos=(5.83013,0.0980762,-77) rot=(0,0,1;1.0472rad)
  shape: bbox 13.66 x 13.66 x 25 mm, 6 faces (baked)
FEATURE [Part::Feature] Box001027039
  Placement = pos=(2.83013,5.09808,-77) rot=(0,0,1;2.0944rad)
  shape: bbox 13.66 x 13.66 x 25 mm, 6 faces (baked)
FEATURE [Part::Feature] Box001027040
  Placement = pos=(-3,5,-77) rot=(0,0,1;3.14159rad)
  shape: bbox 10 x 10 x 25 mm, 6 faces (baked)
FEATURE [Part::Feature] Box001027041
  Placement = pos=(-5.83013,-0.0980762,-77) rot=(0,0,1;4.18879rad)
  shape: bbox 13.66 x 13.66 x 25 mm, 6 faces (baked)
FEATURE [Part::Feature] Box001027042
  Placement = pos=(-2.83013,-5.09808,-77) rot=(0,0,-1;1.0472rad)
  shape: bbox 13.66 x 13.66 x 25 mm, 6 faces (baked)
FEATURE [Part::MultiFuse] Fusion110
  Shapes = -> [Box001027,Box001027038,Box001027041,Box001027040,Box001027039,Box001027042]
FEATURE [Part::Cut] Cut062  label="m3-nut-1"
  Base = -> Cylinder064
  Tool = -> Fusion110
FEATURE [Part::Cut] Cut063  label="rocker"
  Base = -> Cut032
  Placement = pos=(0,0,-6) rot=(0,0,1;0rad)
  Tool = -> Cut062
FEATURE [Part::Feature] Part__Feature069023  label="212001001001001"
  Placement = pos=(0,0,-48.5) rot=(0.905883,0.423527,0;3.14159rad)
  shape: bbox 7 x 7 x 0.5 mm, 6 faces (baked)
FEATURE [Part::Feature] Part__Feature069024  label="212001001001002"
  Placement = pos=(0,0,-30) rot=(0.905883,0.423527,0;3.14159rad)
  shape: bbox 7 x 7 x 0.5 mm, 6 faces (baked)
FEATURE [Part::Box] Box001027045177  label="Cube225"
  AttacherType = Attacher::AttachEngine3D
  Height = 20
  Length = 16
  Placement = pos=(-5,0,-30) rot=(0,1,0;0rad)
  Width = 4.5
FEATURE [Part::Box] Box001027045178  label="Cube226"
  AttacherType = Attacher::AttachEngine3D
  Height = 60
  Length = 10
  Placement = pos=(-10,-2,-57) rot=(0,0,1;0rad)
  Width = 4
FEATURE [Part::Cylinder] Cylinder234  label="Cylinder262"
  Angle = 360
  AttacherType = Attacher::AttachEngine3D
  Height = 74
  Placement = pos=(0,0,-62) rot=(0,0,1;0rad)
  Radius = 2
FEATURE [Part::MultiFuse] Fusion112125  label="top-slot-003"
  Placement = pos=(2.5,0,0) rot=(0,0,1;0rad)
  Shapes = -> [Cylinder234,Box001027045178]
FEATURE [Part::Cylinder] Cylinder235  label="rocker-cut004"
  Angle = 360
  AttacherType = Attacher::AttachEngine3D
  Height = 18
  Placement = pos=(0,9,-8) rot=(1,0,0;1.5708rad)
  Radius = 4.2
FEATURE [Part::Cylinder] Cylinder236  label="Cylinder263"
  Angle = 360
  AttacherType = Attacher::AttachEngine3D
  Height = 20
  Placement = pos=(7,11,-26) rot=(1,0,0;1.5708rad)
  Radius = 1.7
FEATURE [Part::Cylinder] Cylinder237  label="Cylinder264"
  Angle = 360
  AttacherType = Attacher::AttachEngine3D
  Height = 20
  Placement = pos=(7,11,-13) rot=(1,0,0;1.5708rad)
  Radius = 1.7
FEATURE [Part::MultiFuse] Fusion112126  label="top-slot-m3-clearance001"
  Shapes = -> [Cylinder236,Cylinder237]
FEATURE [Part::MultiFuse] Fusion112127  label="plate-cuts"
  Shapes = -> [Fusion112125,Cylinder235,Fusion112126]
FEATURE [Part::Cut] Cut217  label="top-slot-plate"
  Base = -> Box001027045177
  Tool = -> Fusion112127
FEATURE [Part::Cylinder] Cylinder243  label="M3-clearance007"
  Angle = 360
  AttacherType = Attacher::AttachEngine3D
  Height = 20
  Placement = pos=(34,5,-14) rot=(1,0,0;1.5708rad)
  Radius = 1.7
FEATURE [Part::Box] Box001027045186  label="Cube233"
  AttacherType = Attacher::AttachEngine3D
  Height = 25
  Length = 40
  Placement = pos=(32,-4.5,-33) rot=(0,1,0;0.366519rad)
  Width = 4.5
FEATURE [Part::Cylinder] Cylinder244  label="cutter-fit-cylinder004"
  Angle = 360
  AttacherType = Attacher::AttachEngine3D
  Height = 21
  Placement = pos=(45,5,-26) rot=(1,0,0;1.5708rad)
  Radius = 3.2
FEATURE [Part::Box] Box001027045187  label="Cube234"
  AttacherType = Attacher::AttachEngine3D
  Height = 44
  Length = 12
  Placement = pos=(28,-2.25,-41) rot=(0,0,1;0rad)
  Width = 31
FEATURE [Part::Box] Box001027045188  label="Cube219-xxx002"
  AttacherType = Attacher::AttachEngine3D
  Height = 15
  Length = 30
  Placement = pos=(-10,-70,-57) rot=(0,0,1;0rad)
  Width = 15
FEATURE [Part::Box] Box001027045189  label="Cube235"
  AttacherType = Attacher::AttachEngine3D
  Height = 24
  Length = 47
  Placement = pos=(-5,-4.5,-34) rot=(0,1,0;0rad)
  Width = 4.5
FEATURE [Part::MultiFuse] Fusion112132  label="move-arm-019"
  Shapes = -> [Box001027045186,Box001027045189]
FEATURE [Part::Cylinder] Cylinder245  label="M3-clearance008"
  Angle = 360
  AttacherType = Attacher::AttachEngine3D
  Height = 20
  Placement = pos=(34,5,-29) rot=(1,0,0;1.5708rad)
  Radius = 1.7
FEATURE [Part::MultiFuse] Fusion112134  label="M3-clearance-003"
  Shapes = -> [Cylinder243,Cylinder245]
FEATURE [Part::Box] Box001027045190  label="Cube236"
  AttacherType = Attacher::AttachEngine3D
  Height = 10
  Length = 20
  Placement = pos=(29,-6,-9) rot=(0,1,0;0.139626rad)
  Width = 10
FEATURE [Part::Cut] Cut226  label="move-arm-021"
  Base = -> Fusion112132
  Tool = -> Box001027045190
FEATURE [Part::Cut] Cut227  label="move-arm-022"
  Base = -> Cut226
  Tool = -> Cylinder244
FEATURE [Part::Box] Box001027045191  label="Cube237"
  AttacherType = Attacher::AttachEngine3D
  Height = 35
  Length = 46
  Placement = pos=(-7,-7,-36) rot=(0,0,1;0rad)
  Width = 32
FEATURE [Part::Cut] Cut229  label="step-separator"
  Base = -> Box001027045191
  Tool = -> Box001027045187
FEATURE [Part::Feature] Part__Feature069026  label="M6 thread020"
  Placement = pos=(45,-4,-26) rot=(0.935113,0.250563,-0.250563;1.63783rad)
  shape: bbox 10 x 5.798 x 11.55 mm, 23 faces (baked)
FEATURE [Part::MultiFuse] Fusion112133  label="move-arm-023"
  Shapes = -> [Cut227,Part__Feature069026]
FEATURE [Part::Cylinder] Cylinder246  label="bearing-fit-cylinder006"
  Angle = 360
  AttacherType = Attacher::AttachEngine3D
  Height = 21
  Placement = pos=(64,5,-31) rot=(1,0,0;1.5708rad)
  Radius = 4.6
FEATURE [Part::Cut] Cut228  label="move-arm-024"
  Base = -> Fusion112133
  Placement = pos=(-6.44714,0,-21.2943) rot=(0,-1,0;0.314159rad)
  Tool = -> Cylinder246
FEATURE [Part::Cut] Cut225  label="move-arm-020"
  Base = -> Cut228
  Placement = pos=(12.7119,0,18.2598) rot=(0,1,0;0.314159rad)
  Tool = -> Box001027045188
FEATURE [Part::MultiCommon] Common094  label="cutter-extension-4"
  Shapes = -> [Cut225,Cut229]
FEATURE [Part::Cut] Cut230  label="cutter-extension-003"
  Base = -> Common094
  Tool = -> Fusion112134
FEATURE [Part::Box] Box001027045192  label="Cube238"
  AttacherType = Attacher::AttachEngine3D
  Height = 60
  Length = 10
  Placement = pos=(-10,-2,-57) rot=(0,0,1;0rad)
  Width = 4
FEATURE [Part::Cylinder] Cylinder247  label="Cylinder266"
  Angle = 360
  AttacherType = Attacher::AttachEngine3D
  Height = 74
  Placement = pos=(0,0,-62) rot=(0,0,1;0rad)
  Radius = 2
FEATURE [Part::MultiFuse] Fusion112135  label="top-slot-004"
  Placement = pos=(2.5,0,0) rot=(0,0,1;0rad)
  Shapes = -> [Cylinder247,Box001027045192]
FEATURE [Part::Cylinder] Cylinder248  label="Cylinder267"
  Angle = 360
  AttacherType = Attacher::AttachEngine3D
  Height = 20
  Placement = pos=(7,11,-26) rot=(1,0,0;1.5708rad)
  Radius = 1.4
FEATURE [Part::Cylinder] Cylinder249  label="Cylinder268"
  Angle = 360
  AttacherType = Attacher::AttachEngine3D
  Height = 20
  Placement = pos=(7,11,-13) rot=(1,0,0;1.5708rad)
  Radius = 1.4
FEATURE [Part::MultiFuse] Fusion112136  label="top-slot-m3-tap001"
  Shapes = -> [Cylinder248,Cylinder249]
FEATURE [Part::Cylinder] Cylinder250  label="rocker-cut005"
  Angle = 360
  AttacherType = Attacher::AttachEngine3D
  Height = 18
  Placement = pos=(0,9,-8) rot=(1,0,0;1.5708rad)
  Radius = 4.2
FEATURE [Part::Box] Box001027045193  label="Cube239"
  AttacherType = Attacher::AttachEngine3D
  Height = 10
  Length = 30
  Placement = pos=(-10,-7,-40) rot=(0,0,1;0rad)
  Width = 15
FEATURE [Part::Cylinder] Cylinder251  label="Cylinder269"
  Angle = 360
  AttacherType = Attacher::AttachEngine3D
  Height = 30
  Placement = pos=(19.5,2,-45) rot=(0,0,1;0rad)
  Radius = 1.4
FEATURE [Part::Box] Box001027045194  label="Cube240"
  AttacherType = Attacher::AttachEngine3D
  Height = 9
  Length = 13
  Placement = pos=(15,-4.5,-34) rot=(0,0,1;0rad)
  Width = 9.5
FEATURE [Part::Chamfer] Chamfer032
  Base = -> Box001027045194
  Edges = 1 edges r=3: [Edge6]
FEATURE [Part::Fillet] Fillet044  label="stop-block002"
  Base = -> Chamfer032
  Edges = 2 edges r=2: [Edge2,Edge9]
FEATURE [Part::MultiFuse] Fusion112137  label="extension-holes"
  Shapes = -> [Fusion112135,Fusion112136,Cylinder250,Box001027045193]
FEATURE [Part::Cut] Cut231  label="stop-block"
  Base = -> Fillet044
  Tool = -> Cylinder251
FEATURE [Part::Cut] Cut232  label="cutting-arm-extension-1"
  Base = -> Cut230
  Tool = -> Fusion112137
FEATURE [Part::MultiFuse] Fusion112138  label="cutting-arm-extension"
  Shapes = -> [Cut232,Cut231]
FEATURE [Part::Cylinder] Cylinder252  label="Cylinder270"
  Angle = 360
  AttacherType = Attacher::AttachEngine3D
  Height = 50
  Placement = pos=(23,18,-19) rot=(1,0,0;1.5708rad)
  Radius = 1.7
FEATURE [Part::Cylinder] Cylinder253  label="Cylinder271"
  Angle = 360
  AttacherType = Attacher::AttachEngine3D
  Height = 10
  Placement = pos=(19,10.2,-19) rot=(1,0,0;1.5708rad)
  Radius = 4
FEATURE [Part::Cylinder] Cylinder254  label="Cylinder272"
  Angle = 360
  AttacherType = Attacher::AttachEngine3D
  Height = 30
  Placement = pos=(23,36,-19) rot=(1,0,0;1.5708rad)
  Radius = 2.5
FEATURE [Part::MultiFuse] Fusion112140
  Placement = pos=(-4,0,0) rot=(0,0,1;0rad)
  Shapes = -> [Cylinder252,Cylinder254]
FEATURE [Part::Cylinder] Cylinder257  label="Cylinder275"
  Angle = 360
  AttacherType = Attacher::AttachEngine3D
  Height = 30
  Placement = pos=(23,36,-19) rot=(1,0,0;1.5708rad)
  Radius = 2.5
FEATURE [Part::Cylinder] Cylinder258  label="Cylinder276"
  Angle = 360
  AttacherType = Attacher::AttachEngine3D
  Height = 50
  Placement = pos=(23,18,-19) rot=(1,0,0;1.5708rad)
  Radius = 1.7
FEATURE [Part::MultiFuse] Fusion112142
  Shapes = -> [Cylinder258,Cylinder257]
FEATURE [Part::Mirroring] Part__Mirroring016  label="LED-hole-1"
  Base = (0,0,0)
  Normal = (0,1,0)
  Placement = pos=(-4,0,0) rot=(0,0,1;0rad)
  Source = -> Fusion112142
FEATURE [Part::Cut] Cut234
  Base = -> Box001027045174
  Tool = -> Fusion112123
FEATURE [Part::Cylinder] Cylinder259  label="Cylinder277"
  Angle = 360
  AttacherType = Attacher::AttachEngine3D
  Height = 20
  Placement = pos=(22.4783,-6,-9.9062) rot=(0.989133,0.103962,-0.103962;1.58172rad)
  Radius = 2.5
FEATURE [Part::Cylinder] Cylinder260  label="Cylinder278"
  Angle = 360
  AttacherType = Attacher::AttachEngine3D
  Height = 5.7
  Placement = pos=(19,10.2,-19) rot=(1,0,0;1.5708rad)
  Radius = 4
FEATURE [Part::MultiFuse] Fusion112143
  Shapes = -> [Chamfer029,Cylinder253]
FEATURE [Part::Cut] Cut235  label="bearing-support-2-with-photoT"
  Base = -> Fusion112143
  Tool = -> Fusion112140
FEATURE [Part::Mirroring] Part__Mirroring017  label="Cylinder278 (Mirror #7)"
  Base = (0,0,0)
  Normal = (0,1,0)
  Source = -> Cylinder260
FEATURE [Part::Cylinder] Cylinder261  label="Cylinder279"
  Angle = 360
  AttacherType = Attacher::AttachEngine3D
  Height = 5.7
  Placement = pos=(22.4783,10.2,-9.9062) rot=(0.989133,0.103962,-0.103962;1.58172rad)
  Radius = 4
FEATURE [Part::Mirroring] Part__Mirroring018  label="Cylinder279 (Mirror #8)"
  Base = (0,0,0)
  Normal = (0,1,0)
  Source = -> Cylinder261
FEATURE [Part::Cylinder] Cylinder262  label="Cylinder280"
  Angle = 360
  AttacherType = Attacher::AttachEngine3D
  Height = 30
  Placement = pos=(22.4783,12.2,-9.9062) rot=(0.989133,0.103962,-0.103962;1.58172rad)
  Radius = 1.7
FEATURE [Part::MultiFuse] Fusion112144
  Shapes = -> [Part__Mirroring018,Part__Mirroring017]
FEATURE [Part::MultiFuse] Fusion112145  label="plate-w-LED-blanks"
  Shapes = -> [Fusion112144,Cut234]
FEATURE [Part::MultiFuse] Fusion112146  label="LED-hole-2"
  Shapes = -> [Cylinder259,Cylinder262]
FEATURE [Part::Cylinder] Cylinder263  label="Cylinder281"
  Angle = 360
  AttacherType = Attacher::AttachEngine3D
  Height = 30
  Placement = pos=(23,36,-19) rot=(1,0,0;1.5708rad)
  Radius = 2.5
FEATURE [Part::Cylinder] Cylinder264  label="Cylinder282"
  Angle = 360
  AttacherType = Attacher::AttachEngine3D
  Height = 50
  Placement = pos=(23,18,-19) rot=(1,0,0;1.5708rad)
  Radius = 1.7
FEATURE [Part::MultiFuse] Fusion112147
  Shapes = -> [Cylinder264,Cylinder263]
FEATURE [Part::Mirroring] Part__Mirroring019  label="LED-hole-003"
  Base = (0,0,0)
  Normal = (0,1,0)
  Placement = pos=(-4,0,0) rot=(0,0,1;0rad)
  Source = -> Fusion112147
FEATURE [Part::Cylinder] Cylinder265  label="Cylinder283"
  Angle = 360
  AttacherType = Attacher::AttachEngine3D
  Height = 30
  Placement = pos=(22.4783,12.2,-9.9062) rot=(0.989133,0.103962,-0.103962;1.58172rad)
  Radius = 1.7
FEATURE [Part::Cylinder] Cylinder266  label="Cylinder284"
  Angle = 360
  AttacherType = Attacher::AttachEngine3D
  Height = 20
  Placement = pos=(22.4783,-6,-9.9062) rot=(0.989133,0.103962,-0.103962;1.58172rad)
  Radius = 2.5
FEATURE [Part::MultiFuse] Fusion112148  label="LED-hole-004"
  Shapes = -> [Cylinder266,Cylinder265]
FEATURE [Part::MultiFuse] Fusion112149  label="LED-holes-1"
  Shapes = -> [Fusion112146,Part__Mirroring016]
FEATURE [Part::MultiFuse] Fusion112150
  Shapes = -> [Part__Mirroring019,Fusion112148]
FEATURE [Part::Cut] Cut236  label="clamp-plate-with-LEDs"
  Base = -> Fusion112145
  Tool = -> Fusion112149
FEATURE [Part::Box] Box001027045195  label="Cube241"
  AttacherType = Attacher::AttachEngine3D
  Height = 10
  Length = 10
  Placement = pos=(17,-4.5,-13) rot=(0,0,1;0rad)
  Width = 4.5
FEATURE [Part::Fillet] Fillet
  Base = -> Box001027045195
  Edges = 2 edges r=3.5: [Edge2,Edge6]
FEATURE [Part::MultiFuse] Fusion112151
  Shapes = -> [Fusion112138,Fillet]
FEATURE [Part::Cut] Cut237  label="cutting-arm-extension-with-photoT"
  Base = -> Fusion112151
  Tool = -> Fusion112150
FEATURE [Part::Box] Box001027045196  label="Cube242"
  AttacherType = Attacher::AttachEngine3D
  Height = 20
  Length = 4
  Placement = pos=(70,3,-49) rot=(0,0,1;0rad)
  Width = 9
FEATURE [Part::Box] Box001027045197  label="Cube243"
  AttacherType = Attacher::AttachEngine3D
  Height = 16
  Length = 10
  Placement = pos=(70,7,-47) rot=(0,0,1;0rad)
  Width = 3
FEATURE [Part::Box] Box001027045198  label="Cube244"
  AttacherType = Attacher::AttachEngine3D
  Height = 15
  Length = 10
  Placement = pos=(63,7.25,-46.5) rot=(0,0,1;0rad)
  Width = 2.5
FEATURE [Part::MultiFuse] Fusion112152  label="pin-strip-hole"
  Placement = pos=(2,0,0) rot=(0,0,1;0rad)
  Shapes = -> [Box001027045197,Box001027045198]
FEATURE [Part::Cut] Cut238  label="pin-strip-bracket"
  Base = -> Box001027045196
  Tool = -> Fusion112152
FEATURE [Part::MultiFuse] Fusion112153  label="bearing-support-02"
  Shapes = -> [Cut235,Cut238]
FEATURE [Part::Box] Box001027045199  label="Cube245"
  AttacherType = Attacher::AttachEngine3D
  Height = 8
  Length = 3
  Width = 8
FEATURE [Part::Cylinder] Cylinder267  label="Cylinder285"
  Angle = 360
  AttacherType = Attacher::AttachEngine3D
  Height = 10
  Placement = pos=(-3,4,4.5) rot=(0,1,0;1.5708rad)
  Radius = 2
FEATURE [Part::Fillet] Fillet045
  Base = -> Box001027045199
  Edges = 2 edges r=3: [Edge10,Edge12]
FEATURE [Part::Cut] Cut239  label="cable-tie-holder-1"
  Base = -> Fillet045
  Placement = pos=(25,-4,10) rot=(0,1,0;1.5708rad)
  Tool = -> Cylinder267
FEATURE [Part::Cut] Cut240  label="cable-tie-holder-002"
  Base = -> Fillet045
  Placement = pos=(31,-7,-24) rot=(1,0,0;1.5708rad)
  Tool = -> Cylinder267
FEATURE [Part::Cut] Cut241  label="cable-tie-holder-003"
  Base = -> Fillet045
  Placement = pos=(58,4,-20) rot=(-1,0,0;1.5708rad)
  Tool = -> Cylinder267
FEATURE [Part::MultiFuse] Fusion112154  label="gearbox"
  Shapes = -> [Chamfer014,Cut239]
FEATURE [App::DocumentObjectGroup] Group  label="Drive"
  Group = -> [Cut002,Fusion048,Part__Feature035,Part__Feature066,Cylinder013,Part__Feature067,Cut004,Cylinder069,Chamfer011,Cut063,Part__Feature069023,Part__Feature069024,Fusion112154]
FEATURE [Part::MultiFuse] Fusion112155  label="clamp-plate"
  Shapes = -> [Cut236,Cut240]
FEATURE [App::DocumentObjectGroup] Group004  label="Moving-arm"
  Group = -> [Fillet041,Cut217,Cut237,Fusion112155]
FEATURE [Part::MultiFuse] Fusion112156  label="bearing-support-2"
  Shapes = -> [Fusion112153,Cut241]
FEATURE [App::DocumentObjectGroup] Group005  label="Stationary-arm"
  Group = -> [Chamfer027,Chamfer028,Fusion112156]
